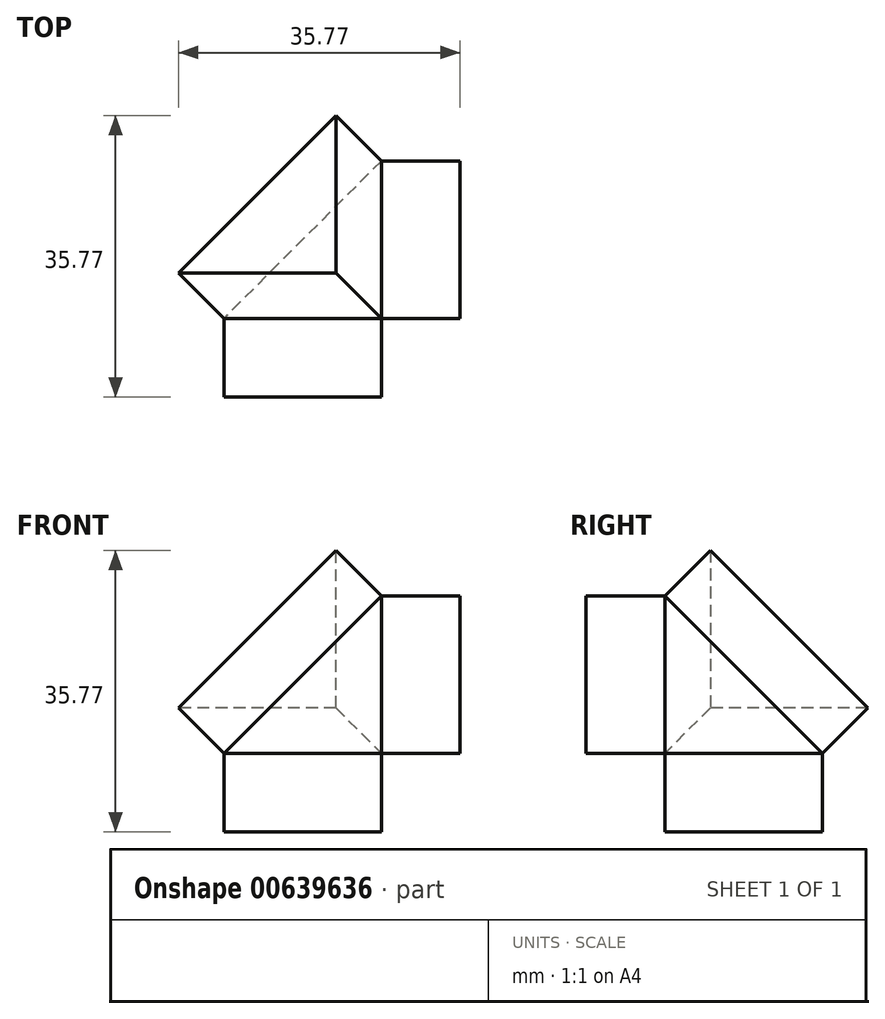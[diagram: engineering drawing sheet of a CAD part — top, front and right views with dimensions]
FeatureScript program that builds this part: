
annotation { "Feature Type Name" : "Feature", "Feature Type Description" : "" }
export const myFeature = defineFeature(function(context is Context, id is Id, definition is map)
    precondition{}
    {
        {
            var Q0;
            Q0=qCreatedBy(makeId("Top.planeOp"),FACE);
            var sketch = newSketch(context, id + "F0", { "sketchPlane" : qUnion([Q0])});
            skLineSegment(sketch, "E0.bottom", {"start": v(10, 10) * mm, "end": v(-10, 10) * mm});
            skLineSegment(sketch, "E0.top", {"start": v(10, -10) * mm, "end": v(-10, -10) * mm});
            skLineSegment(sketch, "E0.left", {"start": v(10, 10) * mm, "end": v(10, -10) * mm});
            skLineSegment(sketch, "E0.right", {"start": v(-10, 10) * mm, "end": v(-10, -10) * mm});
            skPoint(sketch, "E0.middle", {"position": v(0, 0) * mm});
            skSolve(sketch);
        }
        {
            var Q0;
            Q0=makeQuery(id+"F0.imprint","IMPRINT",FACE,{"disambiguationData":[TD([[makeQuery(id+"F0.imprint","IMPRINT",EDGE,{"derivedFrom":sQuery(id+"F0.wireOp",EDGE,"E0.bottom")}),1.0]])]});
            extrude(context, id + "F1", {"entities" : qUnion([Q0]), "depth" : 20 * mm});
        }
        {
            var Q0;
            Q0=makeQuery(id+"F1.opExtrude","SWEPT_EDGE",EDGE,{"disambiguationData":[OSD([sQuery(id+"F0.wireOp",EDGE,"E0.bottom"),sQuery(id+"F0.wireOp",EDGE,"E0.right")])]});
            var Q1;
            Q1=makeQuery(id+"F1.opExtrude","CAP_EDGE",EDGE,{"disambiguationData":[OSD([sQuery(id+"F0.wireOp",EDGE,"E0.right")])],"isStart":false});
            var Q2;
            Q2=makeQuery(id+"F1.opExtrude","CAP_EDGE",EDGE,{"disambiguationData":[OSD([sQuery(id+"F0.wireOp",EDGE,"E0.bottom")])],"isStart":false});
            chamfer(context, id + "F2", {"entities" : qUnion([Q0, Q1, Q2]), "width" : 20 * mm, "tangentPropagation" : true});
        }
        {
            var Q0;
            Q0=makeQuery(id+"F1.opExtrude","SWEPT_FACE",FACE,{"disambiguationData":[OSD([sQuery(id+"F0.wireOp",EDGE,"E0.left")])]});
            var sketch = newSketch(context, id + "F3", { "sketchPlane" : qUnion([Q0])});
            skSolve(sketch);
        }
        {
            var Q0;
            Q0=qSketchRegion(id+"F3",true);
            var Q1;
            {var subQ0=sQuery(id+"F0.wireOp",EDGE,"E0.left");Q1=makeQuery(id+"F3.imprint","IMPRINT",FACE,{"disambiguationData":[TD([[makeQuery(id+"F3.imprint","IMPRINT",EDGE,{"derivedFrom":makeQuery(id+"F1.opExtrude","CAP_EDGE",EDGE,{"disambiguationData":[OSD([subQ0])],"isStart":true})}),-1.0]])]});}
            extrude(context, id + "F4", {"entities" : qUnion([Q0, Q1]), "operationType" : NewBodyOperationType.ADD, "depth" : 10 * mm});
        }
        {
            var Q0;
            {var subQ0=sQuery(id+"F0.wireOp",EDGE,"E0.left");Q0=makeQuery(id+"F4.boolean.opBoolean","MERGE",FACE,{"derivedFrom":[makeQuery(id+"F1.opExtrude","CAP_FACE",FACE,{"disambiguationData":[OSD([sQuery(id+"F0.wireOp",EDGE,"E0.bottom"),sQuery(id+"F0.wireOp",EDGE,"E0.top"),subQ0,sQuery(id+"F0.wireOp",EDGE,"E0.right")])],"isStart":true}),makeQuery(id+"F4.opExtrude","SWEPT_FACE",FACE,{"disambiguationData":[OSD([subQ0])]})]});}
            var sketch = newSketch(context, id + "F5", { "sketchPlane" : qUnion([Q0])});
            skLineSegment(sketch, "E1", {"start": v(10, -10) * mm, "end": v(10, 10) * mm});
            skSolve(sketch);
        }
        {
            var Q0;
            {var subQ0=sQuery(id+"F5.wireOp",EDGE,"E1");Q0=makeQuery(id+"F5.imprint","IMPRINT",FACE,{"disambiguationData":[TD([[makeQuery(id+"F5.imprint","IMPRINT",EDGE,{"derivedFrom":subQ0}),1.0]])]});}
            extrude(context, id + "F6", {"entities" : qUnion([Q0]), "operationType" : NewBodyOperationType.ADD, "depth" : 10 * mm});
        }
        {
            var Q0;
            {var subQ0=sQuery(id+"F0.wireOp",EDGE,"E0.left");var subQ1=sQuery(id+"F0.wireOp",EDGE,"E0.top");Q0=makeQuery(id+"F6.boolean.opBoolean","MERGE",FACE,{"derivedFrom":[makeQuery(id+"F4.boolean.opBoolean","MERGE",FACE,{"derivedFrom":[makeQuery(id+"F1.opExtrude","SWEPT_FACE",FACE,{"disambiguationData":[OSD([subQ1])]}),makeQuery(id+"F4.opExtrude","SWEPT_FACE",FACE,{"disambiguationData":[OSD([subQ1,subQ0])]})]}),makeQuery(id+"F6.opExtrude","SWEPT_FACE",FACE,{"disambiguationData":[OSD([subQ1,subQ0])]})]});}
            var sketch = newSketch(context, id + "F7", { "sketchPlane" : qUnion([Q0])});
            skLineSegment(sketch, "E2", {"start": v(10, 0) * mm, "end": v(-10, 0) * mm});
            skLineSegment(sketch, "E3", {"start": v(10, 0) * mm, "end": v(10, 20) * mm});
            skSolve(sketch);
        }
        {
            var Q0;
            Q0=makeQuery(id+"F7.imprint","IMPRINT",FACE,{"disambiguationData":[TD([[makeQuery(id+"F7.imprint","IMPRINT",EDGE,{"derivedFrom":sQuery(id+"F7.wireOp",EDGE,"E2")}),-1.0]])]});
            extrude(context, id + "F8", {"entities" : qUnion([Q0]), "operationType" : NewBodyOperationType.ADD, "depth" : 10 * mm});
        }
        {
            var Q0;
            Q0=makeQuery(id+"F2.opChamfer","BLEND_FACE",FACE,{"disambiguationData":[OSD([sQuery(id+"F0.wireOp",EDGE,"E0.bottom"),sQuery(id+"F0.wireOp",EDGE,"E0.right")])]});
            extrude(context, id + "F9", {"entities" : qUnion([Q0]), "operationType" : NewBodyOperationType.ADD, "depth" : 10 * mm});
        }
        {
            var Q0;
            Q0=makeQuery(id+"F9.opExtrude","CAP_FACE",FACE,{"disambiguationData":[OSD([sQuery(id+"F0.wireOp",EDGE,"E0.bottom"),sQuery(id+"F0.wireOp",EDGE,"E0.right")])],"isStart":false});
            var sketch = newSketch(context, id + "F10", { "sketchPlane" : qUnion([Q0])});
            skLineSegment(sketch, "E4", {"start": v(0, 0) * mm, "end": v(-12.25, -7.07) * mm});
            skLineSegment(sketch, "E5", {"start": v(12.25, -7.07) * mm, "end": v(12.25, 7.07) * mm});
            skLineSegment(sketch, "E6", {"start": v(12.25, 7.07) * mm, "end": v(4.08, -7.07) * mm});
            skCircle(sketch, "E7", {"center": v(4.08, -7.07) * mm, "radius": 2.5 * mm});
            skSolve(sketch);
        }
        {
            var Q0;
            Q0=sQuery(id+"F10.wireOp",VERTEX,"E7.center");
            var Q1;
            Q1=makeQuery(id+"F1.opExtrude","SWEPT_BODY",BODY,{"disambiguationData":[OSD([sQuery(id+"F0.wireOp",EDGE,"E0.bottom"),sQuery(id+"F0.wireOp",EDGE,"E0.top"),sQuery(id+"F0.wireOp",EDGE,"E0.left"),sQuery(id+"F0.wireOp",EDGE,"E0.right")])]});
            hole(context, id + "F11", {"style" : HoleStyle.SIMPLE, "endStyle" : HoleEndStyle.BLIND, "holeDiameter" : 5 * mm, "majorDiameter" : 5 * mm, "holeDepth" : 7 * mm, "isTappedThrough" : true, "tappedDepth" : 12 * mm, "tapClearance" : 3, "startFromSketch" : true, "locations" : qUnion([Q0]), "scope" : qUnion([Q1])});
        }
    });
